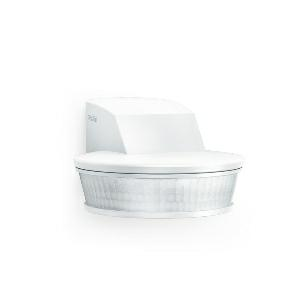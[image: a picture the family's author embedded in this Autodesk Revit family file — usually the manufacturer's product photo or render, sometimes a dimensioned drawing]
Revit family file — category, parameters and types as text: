
# Revit family: sensiq_s_034955
name_source: partatom
category: Elektroinstallationen
revit_build: Autodesk Revit 2016 (Build: 20190508_0715(x64)
units: mm (PartAtom-declared; Revit-internal decimal feet)

## family parameters
Basisbauteil = Fläche
Beim Laden mit Abzugskörper schneiden = Nein
Bemaßung runder Anschluss = Durchmesser verwenden
Beschriftungsausrichtung beibehalten = Nein
Gemeinsam genutzt = Nein
Raumberechnungspunkt = Nein
Teiletyp = Normal

## types (1)
- sensIQ S
    Apparent Load = 0 VA
    Beschreibung = Type: Other; Type of accessory: Corner adapter; Dimensions (L x W x H): 128 x 114 x 74 mm; Mains power supply: 100 – 240 V / 50 – 60 Hz; Power supply, detail: 500 VA max., 120 V; Sensor Technology: passive infrared; Application, place: Indoors, Outdoors; Application, room: multi-storey / underground car park, outdoors, warehouse, front door, all round the building, courtyard & driveway, Indoors; Installation site: wall, corner; Installation: Surface wiring; Switching zones: 1360 switching zones; Electronic scalability: No; Mechanical scalability: Yes; Mounting height: 2,00 – 5,00 m; Optimum mounting height: 2 m; Detection angle: 300 °; Angle of aperture: 90 °; Sneak-by guard: Yes; Capability of masking out individual segments: Yes; Reach, detail: Reach adjustable from 2 - 20 m in 3 directions (100° in each); Reach, radial: r = 4 m (42 m²); Reach, tangential: r = 20 m (1047 m²); Twilight setting TEACH: Yes; Twilight setting: 2 – 2000 lx; Time setting: 5 sec – 15 min; Switching output 1, resistive: 2000 W; Constant-lighting control: No; Basic light level function: No; Functions: Normal / test mode, Manual ON / ON-OFF; Settings via: Remote control, Potentiometers, Smart Remote; With remote control: Yes; Interconnection: Yes; IP-rating: IP54; Material: Plastic; Ambient temperature: -20 – 50 °C; Colour: white; Colour, RAL: 9010; IDs, certificates: VDE; Manufacturer's Warranty: 5 years; Version: white; PU1, EAN: 4007841034955
    Height = 74 mm
    Hersteller = Steinel
    Length = 128 mm
    Maximum range = 22.149 m
    ModVariant = Nein
    Modell = 034955
    Mounting Type = Surface mounted
    Number of Poles = 1
    OnlyDefault = Ja
    Power Factor = 1
    Product Name = sensIQ S
    Product group = Sensor-switched indoor light
    ProductGroupID = 30
    Protection Class = Protection class
    Protection Degree = IP 54
    RlxData = <blob elided: 169117 chars, md5=78202c2c>
    Sensor characteristics = Semi circular 145°-300°
    Sensor type = Passive (infrared)
    SensorDataFile = <blob elided: 9086 chars, md5=cfd8d4b9>
    Type of entry = Motion
    Typenbild = produkt1_034955.jpg
    Typenkommentare = Product without accessories
    URL = http://relux.com
    VarID = ---
    Voltage = 0 V
    Vorgabe-Ansicht = 1800 mm
    Weight = 0.00 kg
    Width = 114 mm

## geometry (parser evidence)
native form markers: Sweep x15
no freeform markers — native parametric forms only
